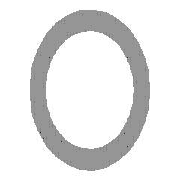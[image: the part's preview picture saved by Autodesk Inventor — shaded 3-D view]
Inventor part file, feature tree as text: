
AUTODESK INVENTOR PART (.ipt)
format: ipt  version: 2013 (Build 170138000, 138)  size: 111,104 bytes
history: native  units: mm (DEFAULTED — no unit token found)
features: other x4, sketch x3, plane x1
ambient origin geometry x8: Origin, YZ Plane, XZ Plane, XY Plane, X Axis, Y Axis, Z Axis, Center Point
bodies: Solid1 (feature_tree), Body (feature_tree)
feature tree (8):
  parser-record x1  (decoder bookkeeping rows leaked as tree rows — omitted from the tree; the rows remain in map.json)
  other  "Driven Length"
  other  "Start plane"
  other  "End plane"
  sketch  "Sketch"  dims[d2=177.8mm d3=0.0mm d4=-0.0mm d5=177.8mm d6=90.0deg d7=177.8mm]
  sketch  "Sketch3"  dims[d0=33.401mm]
  plane  "Work Plane3"
  sketch  "Sketch4"  dims[d1=3.3782mm]
